# Revit family: Cover_Downspout-Zurn-Z199-DC
name_source: partatom
category: Plumbing Fixtures
units: mm (PartAtom-declared; Revit-internal decimal feet)

## family parameters
Cut with Voids When Loaded = No
Host = Face
Maintain Annotation Orientation = No
OmniClass Number = 23.45.55.21
OmniClass Title = Drains (Wastes)
Part Type = Normal
Room Calculation Point = No
Round Connector Dimension = Use Diameter
Shared = No

## types (7) — shared parameters
Assembly Code = D2040300
CW Connection = No
Cover = Steel - Zurn Industries, LLC - Stainless Type 304
Default Elevation = 0' - 0"
Description = Downspout Cover
Frame = Steel - Zurn Industries, LLC - Stainless Type 304
HW Connection = No
Manufacturer = Zurn Industries, LLC
Manufacurer Brand = Zurn
Material main = Stainless steel
Model = Z199-DC
Modified Date = 12/20/24
Product Documentation Link = https://www.zurn.com
Product Installation Sheet URL = https://www.zurn.com
Product Page URL = http://www.zurn.com
Product data url = https://bimobject.com
Type Comments = 10 Inch Pipe Size
URL = www.zurn.com
Vent Connection = No
Waste Connection = Yes

## per-type parameters (varying)
| type | C Dimension | Cover OD | D Dimension | Flange ID | Pipe Outlet Diameter |
| 10 Inch Pipe Size | 0' - 11 1/4" | 0' - 11 21/64" | 1' - 3" | 0' - 11 1/4" | 0' - 10" |
| 12 Inch Pipe Size | 1' - 1 1/4" | 1' - 1 21/64" | 1' - 5" | 1' - 1 1/4" | 1' - 0" |
| 15 Inch Pipe Size | 1' - 4 3/8" | 1' - 4 29/64" | 1' - 8 1/8" | 1' - 4 3/8" | 1' - 3" |
| 3 Inch Pipe Size | 0' - 4 1/8" | 0' - 4 13/64" | 0' - 7 7/8" | 0' - 4 1/8" | 0' - 3" |
| 4 Inch Pipe Size | 0' - 5" | 0' - 5 5/64" | 0' - 8 3/4" | 0' - 5" | 0' - 4" |
| 6 Inch Pipe Size | 0' - 7 1/8" | 0' - 7 13/64" | 0' - 10 7/8" | 0' - 7 1/8" | 0' - 6" |
| 8 Inch Pipe Size | 0' - 9 1/8" | 0' - 9 13/64" | 1' - 0 7/8" | 0' - 9 1/8" | 0' - 8" |

## geometry (parser evidence)
native form markers: Sweep x3
no freeform markers — native parametric forms only
